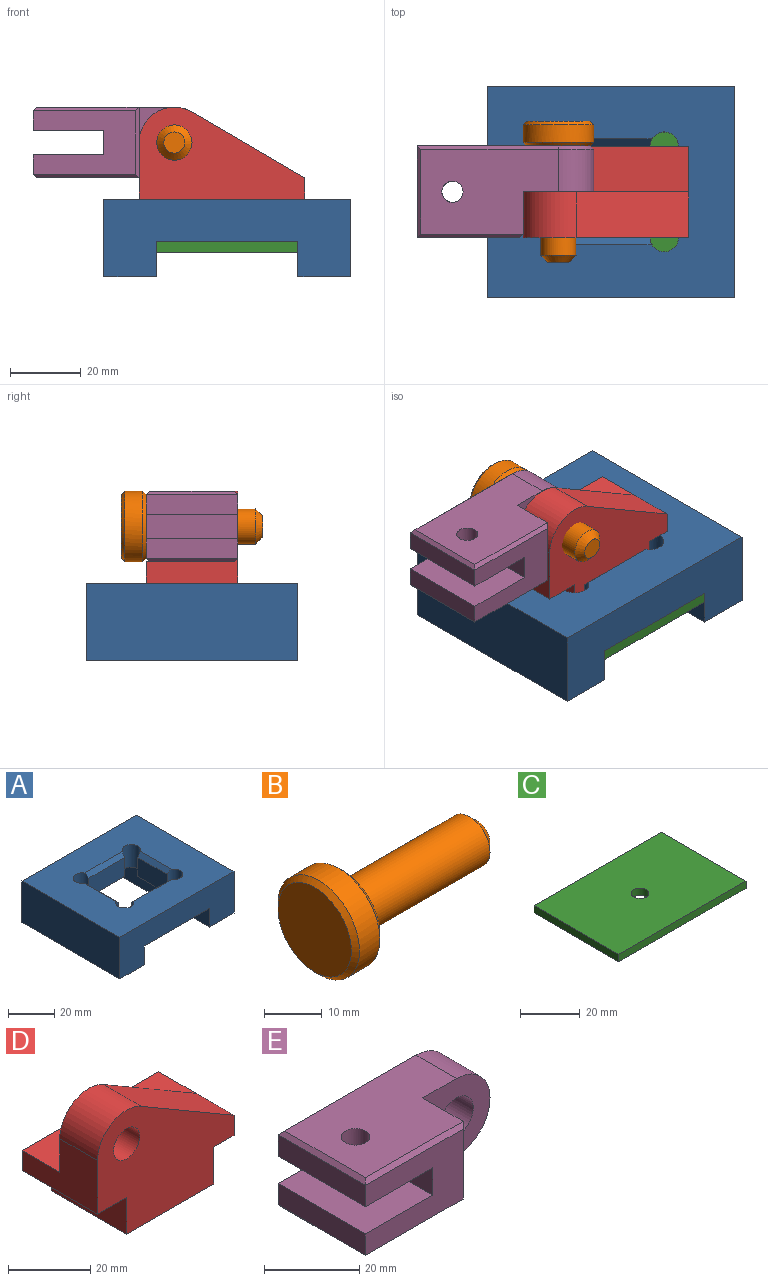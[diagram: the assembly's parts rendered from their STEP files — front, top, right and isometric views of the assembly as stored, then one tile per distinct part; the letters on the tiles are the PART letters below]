
ASSEMBLY  parts=5 mates=4
PART A: 22 faces, bbox 70x60x22 mm
  f0: plane 18x10mm, normal (1,0,0), area 180mm2, adj f1,f7,f17,f20
  f1: cylinder r=4mm len=12mm, axis (0,0,1), area 222.1mm2, adj f0,f2,f16,f17,f19,f20
  f2: plane 22x10mm, normal (0,-1,0), area 220mm2, adj f1,f3,f17,f19
  f3: cylinder r=4mm len=12mm, axis (0,0,1), area 222.1mm2, adj f2,f4,f16,f17,f18,f19
  f4: plane 18x10mm, normal (-1,0,0), area 180mm2, adj f3,f5,f17,f18
  f5: cylinder r=4mm len=12mm, axis (0,0,1), area 222.1mm2, adj f4,f6,f16,f17,f18,f21
  f6: plane 22x10mm, normal (0,1,0), area 220mm2, adj f5,f7,f17,f21
  f7: cylinder r=4mm len=12mm, axis (0,0,1), area 222.1mm2, adj f0,f6,f16,f17,f20,f21
  f8: plane 60x15mm, normal (0,0,-1), area 900mm2, adj f10,f13,f14,f15
  f9: plane 60x15mm, normal (0,0,-1), area 900mm2, adj f11,f12,f13,f15
  f10: plane 60x10mm, normal (-1,0,0), area 600mm2, adj f8,f13,f15,f17
  f11: plane 60x10mm, normal (1,0,0), area 600mm2, adj f9,f13,f15,f17
  f12: plane 60x22mm, normal (-1,0,0), area 1320mm2, adj f9,f13,f15,f16
  f13: plane 70x22mm, normal (0,1,0), area 1140mm2, adj f8,f9,f10,f11,f12,f14,f16,f17
  f14: plane 60x22mm, normal (1,0,0), area 1320mm2, adj f8,f13,f15,f16
  f15: plane 70x22mm, normal (0,-1,0), area 1140mm2, adj f8,f9,f10,f11,f12,f14,f16,f17
  f16: plane 70x60mm, normal (0,0,1), area 3106.4mm2, adj f1,f3,f5,f7,f12,f13,f14,f15
  f17: plane 60x40mm, normal (0,0,-1), area 1469.2mm2, adj f0,f1,f2,f3,f4,f5,f6,f7
  f18: plane 19.07x2mm, normal (-0.71,0,0.71), area 51.9mm2, adj f3,f4,f5,f16
  f19: plane 23.07x2mm, normal (0,-0.71,0.71), area 63.2mm2, adj f1,f2,f3,f16
  f20: plane 19.07x2mm, normal (0.71,0,0.71), area 51.9mm2, adj f0,f1,f7,f16
  f21: plane 23.07x2mm, normal (0,0.71,0.71), area 63.2mm2, adj f5,f6,f7,f16
PART B: 8 faces, bbox 40x20x20 mm
  f0: plane 6x6mm, normal (1,0,0), area 28.3mm2, adj f5
  f1: cylinder r=5mm len=31mm, axis (-1,0,0), area 973.9mm2, adj f2,f5
  f2: plane 18x18mm, normal (1,0,0), area 175.9mm2, adj f1,f7
  f3: cylinder r=10mm len=20mm, axis (-1,0,0), area 314.2mm2, adj f6,f7
  f4: plane 18x18mm, normal (-1,0,0), area 254.5mm2, adj f6
  f5: cone r=5mm half-angle=45deg, axis (-1,0,0), area 71.1mm2, adj f0,f1
  f6: cone r=9mm half-angle=45deg, axis (1,0,0), area 84.4mm2, adj f3,f4
  f7: cone r=10mm half-angle=45deg, axis (-1,0,0), area 84.4mm2, adj f2,f3
PART C: 7 faces, bbox 60x40x3 mm
  f0: cylinder r=3mm len=6mm, axis (0,0,1), area 56.5mm2, adj f5,f6
  f1: plane 40x3mm, normal (1,0,0), area 120mm2, adj f2,f4,f5,f6
  f2: plane 60x3mm, normal (0,1,0), area 180mm2, adj f1,f3,f5,f6
  f3: plane 40x3mm, normal (-1,0,0), area 120mm2, adj f2,f4,f5,f6
  f4: plane 60x3mm, normal (0,-1,0), area 180mm2, adj f1,f3,f5,f6
  f5: plane 60x40mm, normal (0,0,-1), area 2371.7mm2, adj f0,f1,f2,f3,f4
  f6: plane 60x40mm, normal (0,0,1), area 2371.7mm2, adj f0,f1,f2,f3,f4
PART D: 14 faces, bbox 47x26x37 mm
  f0: plane 47x17mm, normal (0,1,0), area 612mm2, adj f1,f2,f3,f4,f5,f6,f9,f10
  f1: plane 26x6mm, normal (1,0,0), area 156mm2, adj f0,f2,f7,f10,f12
  f2: plane 26x7mm, normal (0,0,-1), area 182mm2, adj f0,f1,f3,f12
  f3: plane 26x11mm, normal (1,0,0), area 286mm2, adj f0,f2,f4,f12
  f4: plane 30x26mm, normal (0,0,-1), area 780mm2, adj f0,f3,f5,f12
  f5: plane 26x11mm, normal (-1,0,0), area 286mm2, adj f0,f4,f6,f12
  f6: plane 26x10mm, normal (0,0,-1), area 260mm2, adj f0,f5,f9,f12
  f7: plane 31.96x18.64mm, normal (0.5,0,0.86), area 481mm2, adj f1,f8,f11,f12
  f8: cylinder r=10mm len=15.04mm, axis (0,1,0), area 272.8mm2, adj f7,f9,f11,f12
  f9: plane 26x16mm, normal (-1,0,0), area 286mm2, adj f0,f6,f8,f10,f11,f12
  f10: plane 47x13mm, normal (0,0,1), area 611mm2, adj f0,f1,f9,f11
  f11: plane 47x20mm, normal (0,1,0), area 511.3mm2, adj f7,f8,f9,f10,f13
  f12: plane 47x37mm, normal (0,-1,0), area 1123.3mm2, adj f1,f2,f3,f4,f5,f6,f7,f8
  f13: cylinder r=4.5mm len=13mm, axis (0,1,0), area 367.6mm2, adj f11,f12
PART E: 23 faces, bbox 50x26x20 mm
  f0: cylinder r=3mm len=6.5mm, axis (0,0,1), area 122.5mm2, adj f18,f20
  f1: plane 40x1mm, normal (0,0.71,-0.71), area 55.9mm2, adj f2,f3,f9,f14
  f2: cone r=9mm half-angle=45deg, axis (0,-1,0), area 42.2mm2, adj f1,f4,f9,f13
  f3: plane 26x1mm, normal (-0.71,0,-0.71), area 35.4mm2, adj f1,f5,f14,f15
  f4: plane 40x1mm, normal (0,0.71,0.71), area 55.9mm2, adj f2,f6,f9,f20
  f5: plane 30x1mm, normal (0,-0.71,-0.71), area 41mm2, adj f3,f7,f10,f14
  f6: plane 26x1mm, normal (-0.71,0,0.71), area 35.4mm2, adj f4,f8,f19,f20
  f7: plane 20x1mm, normal (0.71,-0.71,0), area 26.9mm2, adj f5,f8,f10,f12
  f8: plane 30x1mm, normal (0,-0.71,0.71), area 41mm2, adj f6,f7,f10,f20
  f9: plane 49x18mm, normal (0,1,0), area 628.7mm2, adj f1,f2,f4,f15,f16,f17,f18,f19
  f10: plane 29x18mm, normal (0,-1,0), area 382mm2, adj f5,f7,f8,f15,f16,f17,f18,f19
  f11: plane 20x20mm, normal (0,-1,0), area 278.5mm2, adj f12,f13,f14,f20,f22
  f12: plane 20x12mm, normal (1,0,0), area 240mm2, adj f7,f11,f14,f20
  f13: cylinder r=10mm len=20mm, axis (0,1,0), area 377mm2, adj f2,f11,f14,f20
  f14: plane 39x24mm, normal (0,0,-1), area 787.7mm2, adj f1,f3,f5,f11,f12,f13,f21
  f15: plane 26x5.5mm, normal (-1,0,0), area 143mm2, adj f3,f9,f10,f16
  f16: plane 26x20mm, normal (0,0,1), area 491.7mm2, adj f9,f10,f15,f17,f21
  f17: plane 26x7mm, normal (-1,0,0), area 182mm2, adj f9,f10,f16,f18
  f18: plane 26x20mm, normal (0,0,-1), area 491.7mm2, adj f0,f9,f10,f17,f19
  f19: plane 26x5.5mm, normal (-1,0,0), area 143mm2, adj f6,f9,f10,f18
  f20: plane 39x24mm, normal (0,0,1), area 787.7mm2, adj f0,f4,f6,f8,f11,f12,f13
  f21: cylinder r=3mm len=6.5mm, axis (0,0,1), area 122.5mm2, adj f14,f16
  f22: cylinder r=5mm len=13mm, axis (0,1,0), area 408.4mm2, adj f9,f11
PLACE A at identity fixed
PLACE B rot(axis=(-0.71,0.71,0),180deg) t=(-15,20,38)mm
PLACE C rot(axis=(0,0,1),90deg) t=(0,0,7)mm
PLACE D t=(-25,-13,11)mm
PLACE E t=(-55,-13,28)mm
MATE fastened D.f6 <-> A.f7  axis (0,0,1) through (-15,-13,22)mm
MATE fastened B.f1 <-> E.f2  axis (0,-1,0) through (-15,13,38)mm
MATE fastened E.f2 <-> D.f8  axis (0,-1,0) through (-15,0,38)mm
MATE fastened C.f6 <-> A.f17  axis (0,0,1) through (20,-30,10)mm
